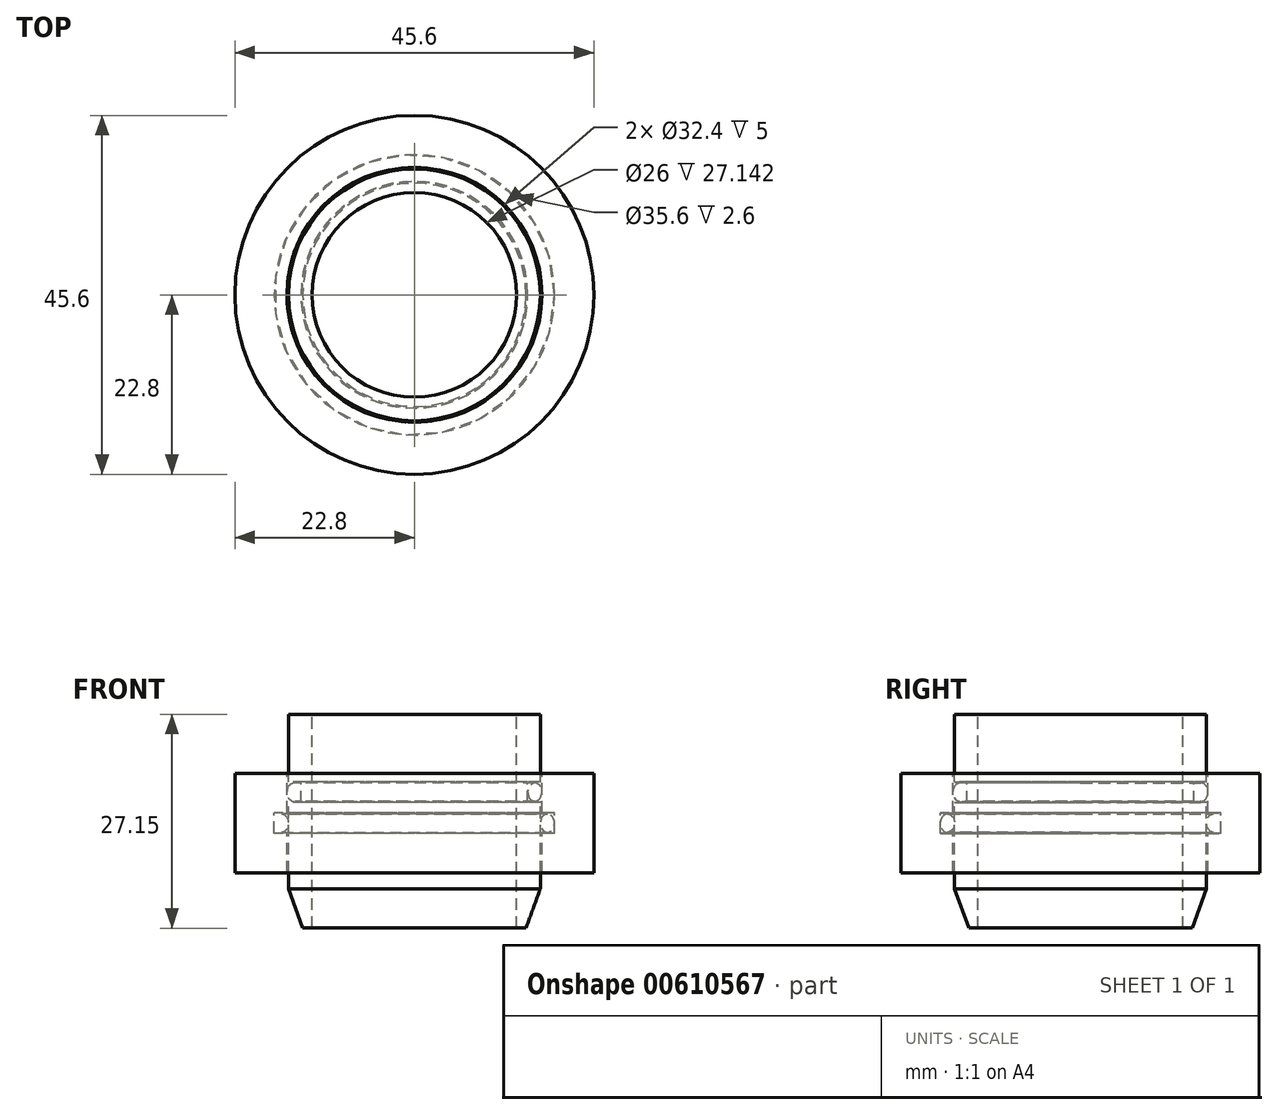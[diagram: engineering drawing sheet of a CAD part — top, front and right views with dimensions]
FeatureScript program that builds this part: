
annotation { "Feature Type Name" : "Feature", "Feature Type Description" : "" }
export const myFeature = defineFeature(function(context is Context, id is Id, definition is map)
    precondition{}
    {
        {
            var Q0;
            Q0=qCreatedBy(makeId("Front.planeOp"),FACE);
            var sketch = newSketch(context, id + "F0", { "sketchPlane" : qUnion([Q0])});
            skLineSegment(sketch, "E0", {"start": v(0, 15.11) * mm, "end": v(0, -16.09) * mm, "construction": true});
            skLineSegment(sketch, "E1", {"start": v(16.2, 0) * mm, "end": v(16.2, 5) * mm});
            skLineSegment(sketch, "E2", {"start": v(16.2, 5) * mm, "end": v(17.8, 5) * mm});
            skLineSegment(sketch, "E3", {"start": v(17.8, 5) * mm, "end": v(17.8, 7.6) * mm});
            skLineSegment(sketch, "E4", {"start": v(17.8, 7.6) * mm, "end": v(16.2, 7.6) * mm});
            skLineSegment(sketch, "E5", {"start": v(16.2, 7.6) * mm, "end": v(16.2, 12.6) * mm});
            skLineSegment(sketch, "E6", {"start": v(16.2, 12.6) * mm, "end": v(22.8, 12.6) * mm});
            skLineSegment(sketch, "E7", {"start": v(22.8, 12.6) * mm, "end": v(22.8, 0) * mm});
            skLineSegment(sketch, "E8", {"start": v(22.8, 0) * mm, "end": v(16.2, 0) * mm});
            skLineSegment(sketch, "E9.bottom", {"start": v(14.18, -7.04) * mm, "end": v(13, -7.04) * mm});
            skLineSegment(sketch, "E9.top", {"start": v(16, 20.1) * mm, "end": v(13, 20.1) * mm});
            skLineSegment(sketch, "E9.left", {"start": v(16, -2.04) * mm, "end": v(16, 8.92) * mm});
            skLineSegment(sketch, "E9.right", {"start": v(13, -7.04) * mm, "end": v(13, 20.1) * mm});
            skLineSegment(sketch, "E10", {"start": v(17.8, 6.3) * mm, "end": v(16, 6.3) * mm, "construction": true});
            skEllipse(sketch, "E11", {"center": v(16.9, 6.3) * mm, "majorRadius": 0.9 * mm, "minorRadius": 1.16 * mm, "majorAxis": v(1, 0)});
            skLineSegment(sketch, "E12", {"start": v(16, 11.52) * mm, "end": v(14.4, 11.52) * mm});
            skLineSegment(sketch, "E13", {"start": v(14.4, 11.52) * mm, "end": v(14.4, 8.92) * mm});
            skLineSegment(sketch, "E14", {"start": v(14.4, 8.92) * mm, "end": v(16, 8.92) * mm});
            skLineSegment(sketch, "E15.trimOffspring", {"start": v(16, 11.52) * mm, "end": v(16, 20.1) * mm});
            skLineSegment(sketch, "E16", {"start": v(14.4, 10.22) * mm, "end": v(16.2, 10.22) * mm, "construction": true});
            skEllipse(sketch, "E17", {"center": v(15.3, 10.22) * mm, "majorRadius": 0.9 * mm, "minorRadius": 1.17 * mm, "majorAxis": v(-1, 0)});
            skLineSegment(sketch, "E18", {"start": v(15.3, 10.22) * mm, "end": v(15.3, 11.39) * mm, "construction": true});
            skLineSegment(sketch, "E19", {"start": v(16.9, 6.3) * mm, "end": v(16.9, 7.47) * mm, "construction": true});
            skLineSegment(sketch, "E20", {"start": v(16, -2.04) * mm, "end": v(14.18, -7.04) * mm});
            skPoint(sketch, "E21.orphan", {"position": v(16, -7.04) * mm});
            skSolve(sketch);
        }
        {
            var Q0;
            Q0=makeQuery(id+"F0.imprint","IMPRINT",FACE,{"disambiguationData":[TD([[makeQuery(id+"F0.imprint","IMPRINT",EDGE,{"derivedFrom":sQuery(id+"F0.wireOp",EDGE,"E1")}),-1.0]])]});
            var Q1;
            {var subQ3=sQuery(id+"F0.wireOp",EDGE,"E9.bottom");Q1=makeQuery(id+"F0.imprint","IMPRINT",FACE,{"disambiguationData":[TD([[makeQuery(id+"F0.imprint","IMPRINT",EDGE,{"derivedFrom":subQ3}),-1.0]])]});}
            var Q2;
            {var subQ0=sQuery(id+"F0.wireOp",EDGE,"E11");var subQ1=makeQuery(id+"F0.imprint","INTERSECT",VERTEX,{"derivedFrom":[sQuery(id+"F0.wireOp",EDGE,"E3"),subQ0]});Q2=makeQuery(id+"F0.imprint","IMPRINT",FACE,{"disambiguationData":[TD([[makeQuery(id+"F0.imprint","IMPRINT",EDGE,{"disambiguationData":[TD([[subQ1,1.0]])],"derivedFrom":subQ0}),1.0]])]});}
            var Q3;
            {var subQ0=sQuery(id+"F0.wireOp",EDGE,"E17");var subQ1=makeQuery(id+"F0.imprint","INTERSECT",VERTEX,{"derivedFrom":[sQuery(id+"F0.wireOp",EDGE,"E5"),subQ0]});Q3=makeQuery(id+"F0.imprint","IMPRINT",FACE,{"disambiguationData":[TD([[makeQuery(id+"F0.imprint","IMPRINT",EDGE,{"disambiguationData":[TD([[subQ1,-1.0]])],"derivedFrom":subQ0}),1.0]])]});}
            var Q4;
            Q4=sQuery(id+"F0.wireOp",EDGE,"E0");
            revolve(context, id + "F1", {"entities" : qUnion([Q0, Q1, Q2, Q3]), "axis" : qUnion([Q4]), "revolveType" : RevolveType.FULL});
        }
    });
